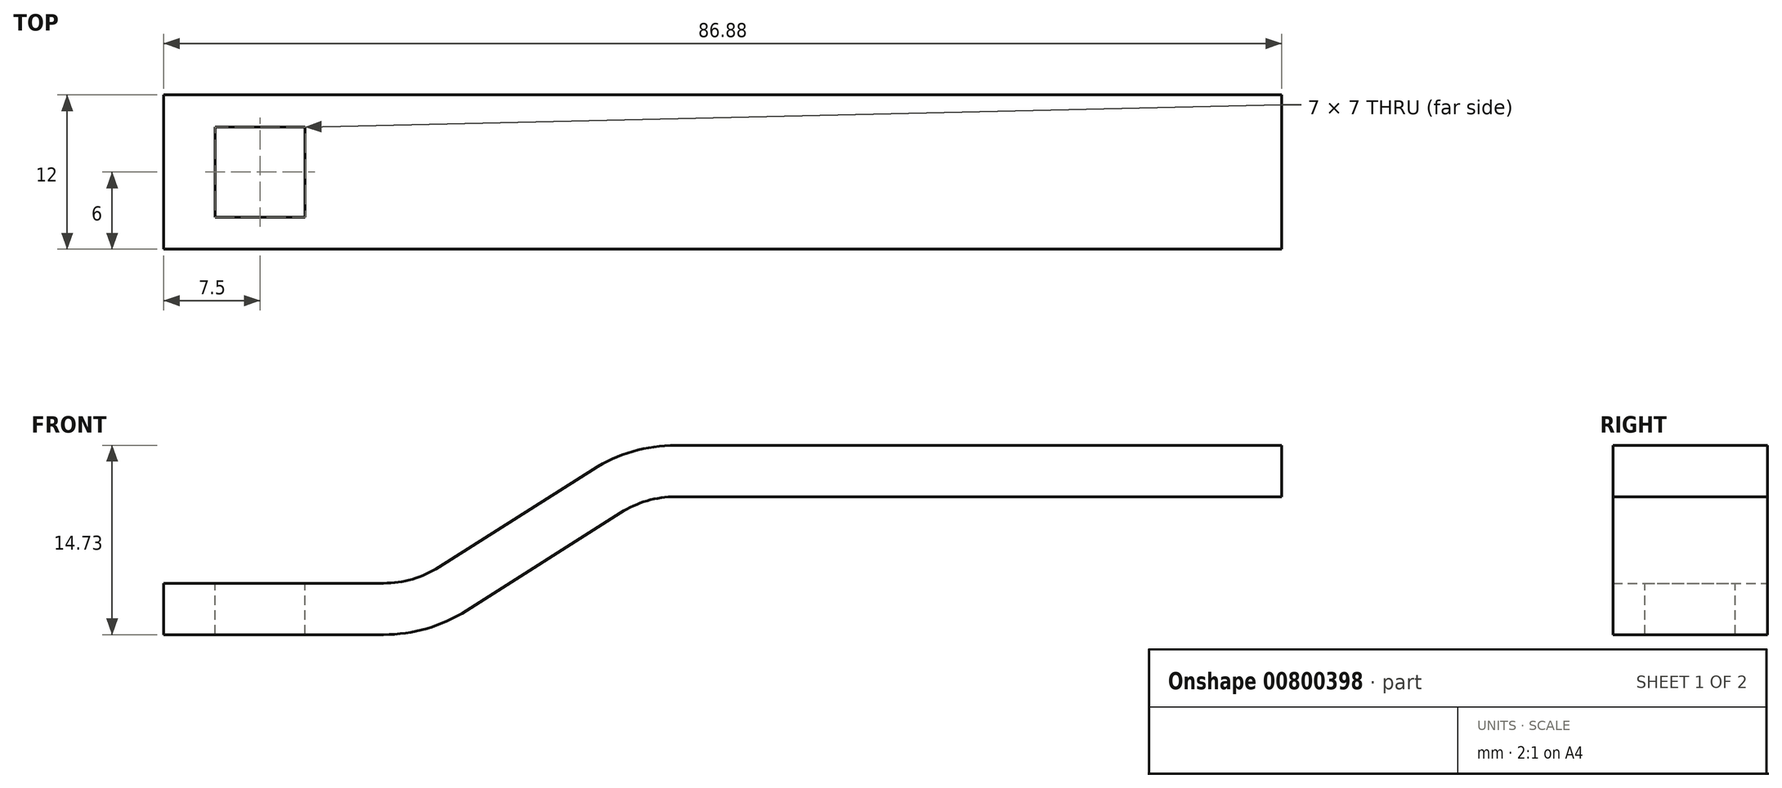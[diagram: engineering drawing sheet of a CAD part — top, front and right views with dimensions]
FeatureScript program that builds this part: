
annotation { "Feature Type Name" : "Feature", "Feature Type Description" : "" }
export const myFeature = defineFeature(function(context is Context, id is Id, definition is map)
    precondition{}
    {
        {
            var Q0;
            Q0=qCreatedBy(makeId("Front.planeOp"),FACE);
            var sketch = newSketch(context, id + "F0", { "sketchPlane" : qUnion([Q0])});
            skLineSegment(sketch, "E0", {"start": v(0, 0) * mm, "end": v(17.1, 0) * mm});
            skLineSegment(sketch, "E1", {"start": v(22.46, 1.56) * mm, "end": v(34.42, 9.17) * mm});
            skLineSegment(sketch, "E2", {"start": v(39.79, 10.73) * mm, "end": v(86.88, 10.73) * mm});
            skPoint(sketch, "E3.visualSharp", {"position": v(20, 0) * mm});
            skArc(sketch, "E3.filletArc", {"start": v(17.1, 0) * mm, "mid": v(19.88, 0.4) * mm, "end": v(22.46, 1.56) * mm});
            skPoint(sketch, "E4.visualSharp", {"position": v(36.88, 10.73) * mm});
            skArc(sketch, "E4.filletArc", {"start": v(39.79, 10.73) * mm, "mid": v(37, 10.33) * mm, "end": v(34.42, 9.17) * mm});
            skSolve(sketch);
        }
        {
            var Q0;
            Q0=qCreatedBy(makeId("Right.planeOp"),FACE);
            var sketch = newSketch(context, id + "F1", { "sketchPlane" : qUnion([Q0])});
            skLineSegment(sketch, "E5.bottom", {"start": v(-6, 2) * mm, "end": v(6, 2) * mm});
            skLineSegment(sketch, "E5.top", {"start": v(-6, -2) * mm, "end": v(6, -2) * mm});
            skLineSegment(sketch, "E5.left", {"start": v(-6, 2) * mm, "end": v(-6, -2) * mm});
            skLineSegment(sketch, "E5.right", {"start": v(6, 2) * mm, "end": v(6, -2) * mm});
            skPoint(sketch, "E5.middle", {"position": v(0, 0) * mm});
            skSolve(sketch);
        }
        {
            var Q0;
            Q0=makeQuery(id+"F1.imprint","IMPRINT",FACE,{"disambiguationData":[TD([[makeQuery(id+"F1.imprint","IMPRINT",EDGE,{"derivedFrom":sQuery(id+"F1.wireOp",EDGE,"E5.bottom")}),-1.0]])]});
            var Q1;
            Q1 = qConstructionFilter(qBodyType(qCreatedBy(id + "F0" ,EDGE), BodyType.WIRE), ConstructionObject.NO);
            sweep(context, id + "F2", {"profiles" : qUnion([Q0]), "path" : qUnion([Q1])});
        }
        {
            var Q0;
            Q0=makeQuery(id+"F2.opSweep","SWEPT_FACE",FACE,{"disambiguationData":[OSD([sQuery(id+"F0.wireOp",EDGE,"E0"),sQuery(id+"F1.wireOp",EDGE,"E5.bottom")])]});
            var sketch = newSketch(context, id + "F3", { "sketchPlane" : qUnion([Q0])});
            skLineSegment(sketch, "E6.bottom", {"start": v(4, -3.5) * mm, "end": v(11, -3.5) * mm});
            skLineSegment(sketch, "E6.top", {"start": v(4, 3.5) * mm, "end": v(11, 3.5) * mm});
            skLineSegment(sketch, "E6.left", {"start": v(4, -3.5) * mm, "end": v(4, 3.5) * mm});
            skLineSegment(sketch, "E6.right", {"start": v(11, -3.5) * mm, "end": v(11, 3.5) * mm});
            skSolve(sketch);
        }
        {
            var Q0;
            Q0 = qSketchRegion(id + "F3", true);
            var Q1;
            Q1=makeQuery(id+"F2.opSweep","SWEPT_FACE",FACE,{"disambiguationData":[OSD([sQuery(id+"F0.wireOp",EDGE,"E0"),sQuery(id+"F1.wireOp",EDGE,"E5.top")])]});
            var Q2;
            Q2=makeQuery(id+"F2.opSweep","SWEPT_BODY",BODY,{"disambiguationData":[OSD([sQuery(id+"F0.wireOp",EDGE,"E0"),sQuery(id+"F1.wireOp",EDGE,"E5.bottom"),sQuery(id+"F1.wireOp",EDGE,"E5.top"),sQuery(id+"F1.wireOp",EDGE,"E5.left"),sQuery(id+"F1.wireOp",EDGE,"E5.right")])]});
            extrude(context, id + "F4", {"entities" : qUnion([Q0]), "operationType" : NewBodyOperationType.REMOVE, "endBound" : BoundingType.UP_TO_BODY, "oppositeDirection" : true, "depth" : 25 * mm, "endBoundEntityFace" : qUnion([Q1]), "endBoundEntityBody" : qUnion([Q2]), "offsetDistance" : 25 * mm});
        }
    });
